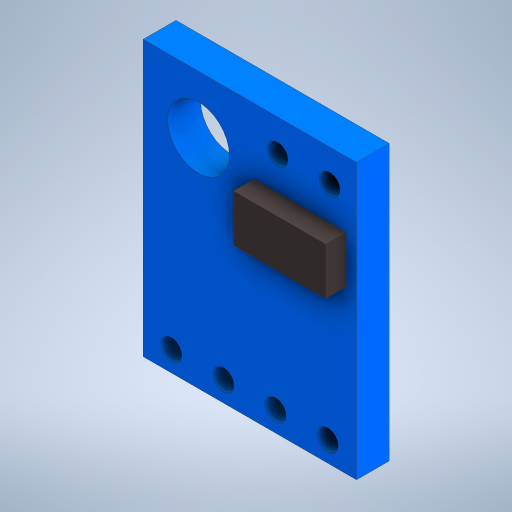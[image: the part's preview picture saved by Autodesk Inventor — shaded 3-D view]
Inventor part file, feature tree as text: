
AUTODESK INVENTOR PART (.ipt)
format: ipt  version: 2023 (Build 270158000, 158)  size: 285,184 bytes
history: native  units: in
note: dims shown in document units (in); Inventor stores cm internally (conversion verified against a paired STEP export)
features: sketch x4, extrude x2, hole x2
ambient origin geometry x8: Origin, YZ Plane, XZ Plane, XY Plane, X Axis, Y Axis, Z Axis, Center Point
bodies: Solid1 (feature_tree)
feature tree (8):
  extrude  "Extrusion1"  Depth=0.5276in
  hole  "Hole1"  [1 undecoded]
  hole  "Hole2"  [1 undecoded]
  extrude  "Extrusion2"  Depth=0.0394in
  sketch  "Sketch1"  dims[d0=0.4094in d1=0.5276in]
  sketch  "Sketch2"  dims[d2=0.063in d3=0.0in d4=0.1102in]
  sketch  "Sketch3"  dims[d5=0.1063in]
  sketch  "Sketch4"  dims[d6=0.1181in d7=0.2362in d8=0.1575in d9=0.0787in d10=90.0deg d11=0.315in d12=0.0in d13=0.1in d14=0.1in d15=0.1in d16=0.0547in d17=0.1in d18=0.0512in d19=0.0394in d20=0.0394in d21=0.2362in d22=0.1575in d23=0.0787in d24=90.0deg d25=0.315in d26=0.0in d27=0.1772in d28=0.0906in d29=0.0197in d30=0.126in d31=0.0394in d32=0.0in]
note: 2 required parameter values undecoded (feature->parameter linkage not recoverable at this tier; creation-order binding heuristic only, values carry confidence <= 0.55)
